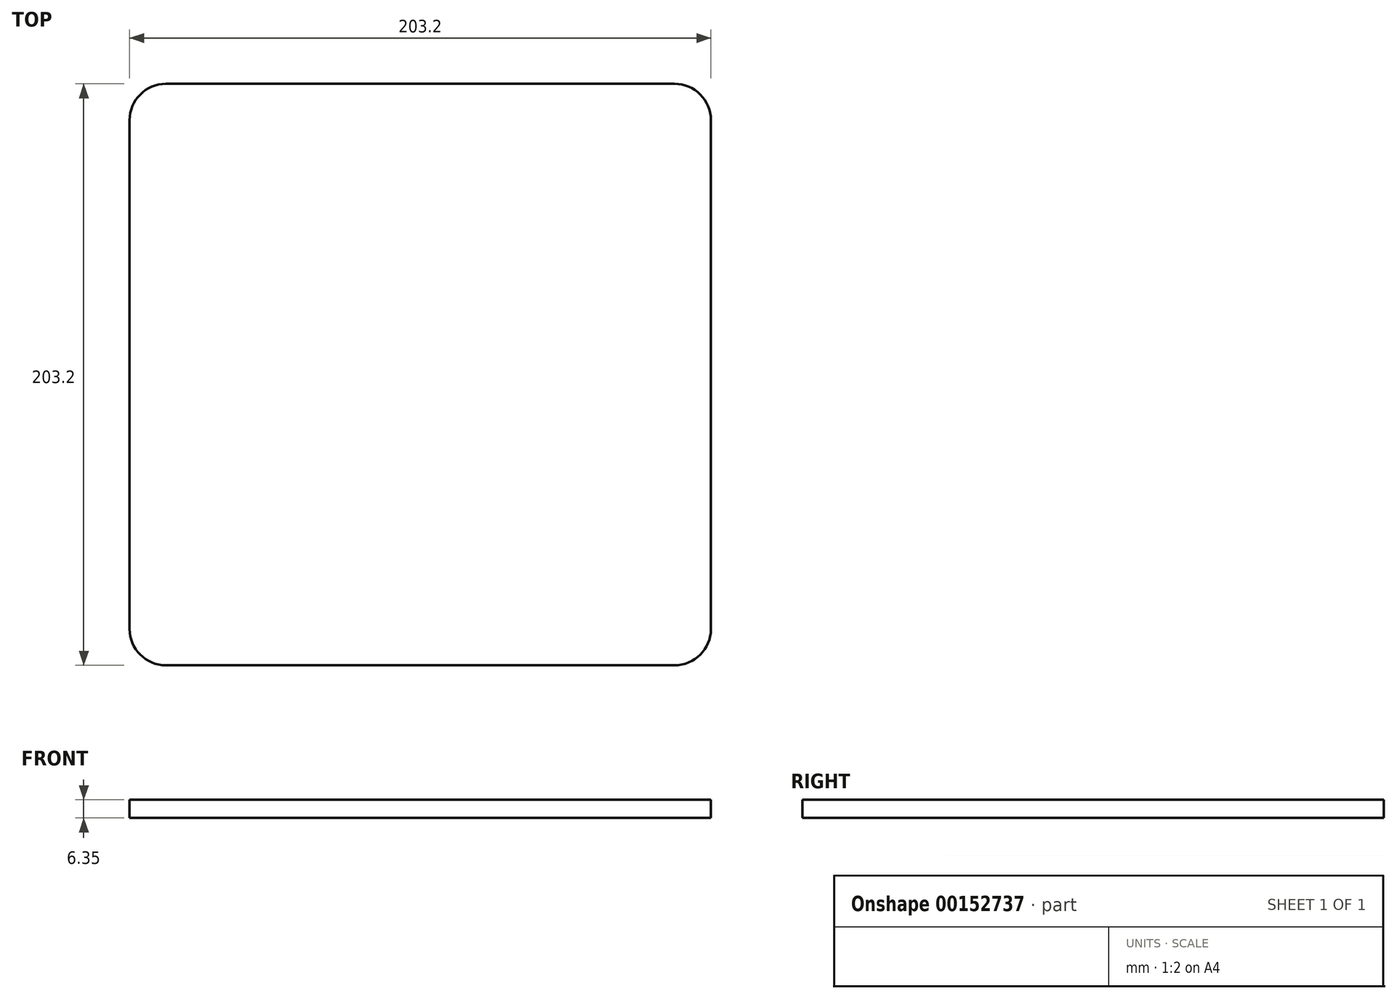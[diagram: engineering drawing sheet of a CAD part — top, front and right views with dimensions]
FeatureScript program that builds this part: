
annotation { "Feature Type Name" : "Feature", "Feature Type Description" : "" }
export const myFeature = defineFeature(function(context is Context, id is Id, definition is map)
    precondition{}
    {
        {
            var Q0;
            Q0=qCreatedBy(makeId("Top.planeOp"),FACE);
            var sketch = newSketch(context, id + "F0", { "sketchPlane" : qUnion([Q0])});
            skLineSegment(sketch, "E0.bottom", {"start": v(101.6, 101.6) * mm, "end": v(-101.6, 101.6) * mm});
            skLineSegment(sketch, "E0.top", {"start": v(101.6, -101.6) * mm, "end": v(-101.6, -101.6) * mm});
            skLineSegment(sketch, "E0.left", {"start": v(101.6, 101.6) * mm, "end": v(101.6, -101.6) * mm});
            skLineSegment(sketch, "E0.right", {"start": v(-101.6, 101.6) * mm, "end": v(-101.6, -101.6) * mm});
            skPoint(sketch, "E0.middle", {"position": v(0, 0) * mm});
            skSolve(sketch);
        }
        {
            var Q0;
            Q0 = qSketchRegion(id + "F0", true);
            extrude(context, id + "F1", {"entities" : qUnion([Q0]), "depth" : 6.35 * mm});
        }
        {
            var Q0;
            Q0=makeQuery(id+"F1.opExtrude","SWEPT_EDGE",EDGE,{"disambiguationData":[OSD([sQuery(id+"F0.wireOp",EDGE,"E0.top"),sQuery(id+"F0.wireOp",EDGE,"E0.right")])]});
            var Q1;
            Q1=makeQuery(id+"F1.opExtrude","SWEPT_EDGE",EDGE,{"disambiguationData":[OSD([sQuery(id+"F0.wireOp",EDGE,"E0.top"),sQuery(id+"F0.wireOp",EDGE,"E0.left")])]});
            var Q2;
            Q2=makeQuery(id+"F1.opExtrude","SWEPT_EDGE",EDGE,{"disambiguationData":[OSD([sQuery(id+"F0.wireOp",EDGE,"E0.bottom"),sQuery(id+"F0.wireOp",EDGE,"E0.left")])]});
            var Q3;
            Q3=makeQuery(id+"F1.opExtrude","SWEPT_EDGE",EDGE,{"disambiguationData":[OSD([sQuery(id+"F0.wireOp",EDGE,"E0.bottom"),sQuery(id+"F0.wireOp",EDGE,"E0.right")])]});
            fillet(context, id + "F2", {"entities" : qUnion([Q0, Q1, Q2, Q3]), "radius" : 12.7 * mm, "tangentPropagation" : true, "allowEdgeOverflow" : false});
        }
    });
